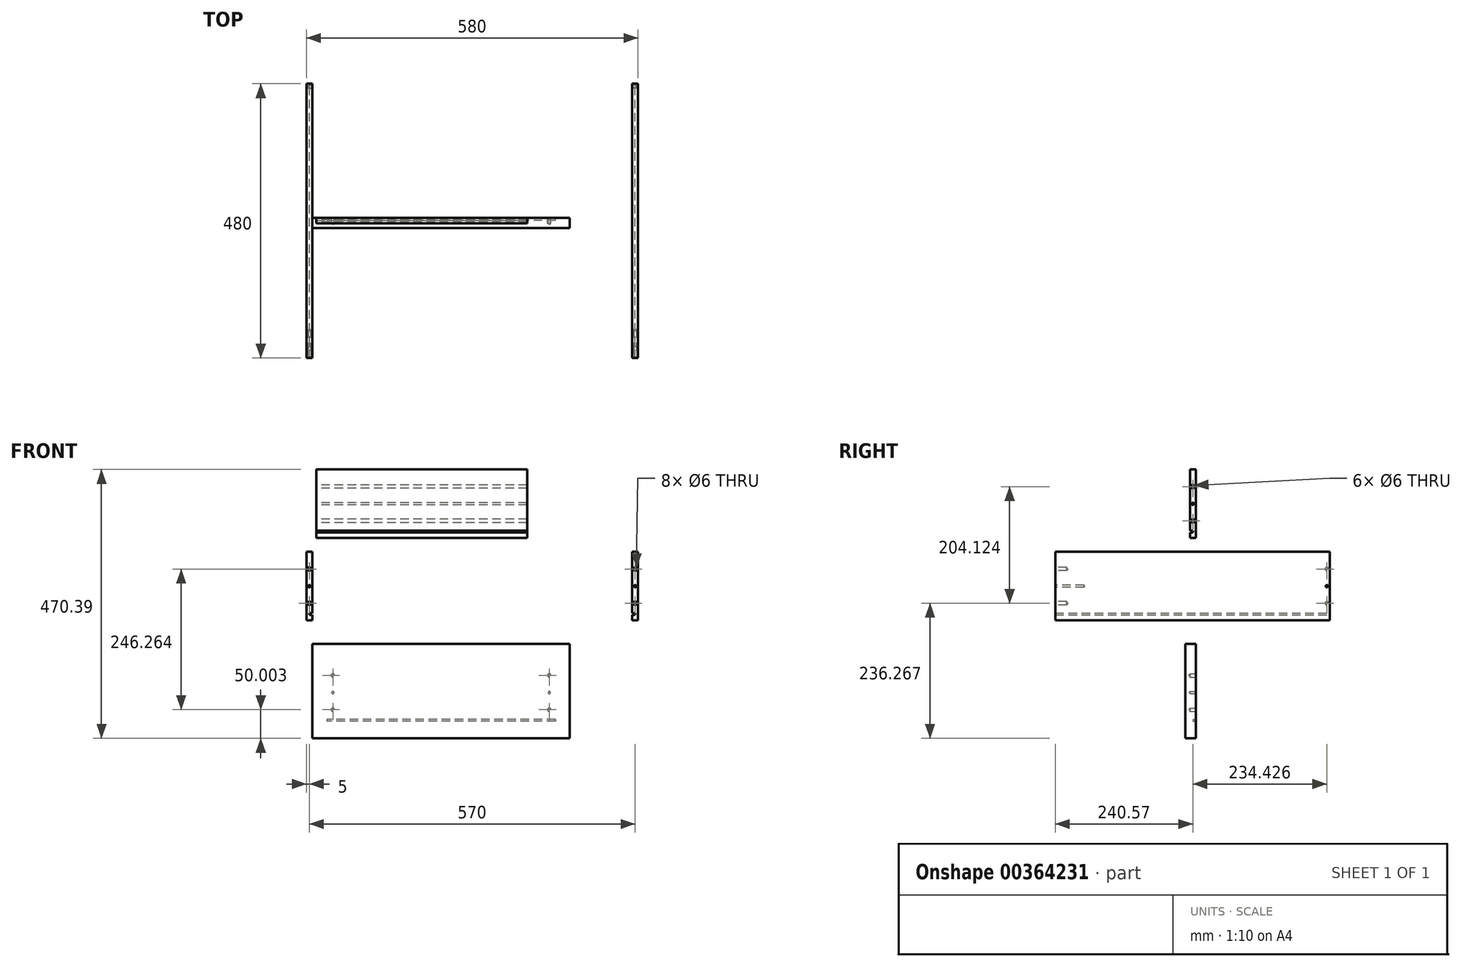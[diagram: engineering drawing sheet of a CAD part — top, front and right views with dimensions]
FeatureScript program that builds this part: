
annotation { "Feature Type Name" : "Feature", "Feature Type Description" : "" }
export const myFeature = defineFeature(function(context is Context, id is Id, definition is map)
    precondition{}
    {
        {
            var Q0;
            Q0=qCreatedBy(makeId("Front.planeOp"),FACE);
            var sketch = newSketch(context, id + "F0", { "sketchPlane" : qUnion([Q0])});
            skLineSegment(sketch, "E0", {"start": v(553.87, 203.2) * mm, "end": v(553.87, 200.2) * mm});
            skText(sketch, "E1", { "text": "Grubość Rowka", "fontName": "OpenSans-Regular.ttf"});
            const initialGuessF0  = {"E1": [0.56755, 0.19197, 1, 0, 0.02]};
            skSetInitialGuess(sketch, initialGuessF0);
            skSolve(sketch);
        }
        {
            var Q0;
            Q0=qCreatedBy(makeId("Right.planeOp"),FACE);
            var sketch = newSketch(context, id + "F1", { "sketchPlane" : qUnion([Q0])});
            skLineSegment(sketch, "E2.bottom", {"start": v(-245.57, 66.34) * mm, "end": v(234.43, 66.34) * mm});
            skLineSegment(sketch, "E2.top", {"start": v(-245.57, -53.66) * mm, "end": v(234.43, -53.66) * mm});
            skLineSegment(sketch, "E2.left", {"start": v(-245.57, 66.34) * mm, "end": v(-245.57, -53.66) * mm});
            skLineSegment(sketch, "E2.right", {"start": v(234.43, 66.34) * mm, "end": v(234.43, -53.66) * mm});
            skSolve(sketch);
        }
        {
            var Q0;
            Q0 = qSketchRegion(id + "F1", true);
            extrude(context, id + "F2", {"entities" : qUnion([Q0]), "depth" : -290 * mm, "hasSecondDirection" : true, "secondDirectionOppositeDirection" : true, "secondDirectionDepth" : 280 * mm});
        }
        {
            var Q0;
            Q0=qCreatedBy(makeId("Right.planeOp"),FACE);
            var sketch = newSketch(context, id + "F3", { "sketchPlane" : qUnion([Q0])});
            skLineSegment(sketch, "E3.bottom", {"start": v(-245.57, -40.66) * mm, "end": v(234.43, -40.66) * mm});
            skLineSegment(sketch, "E3.top", {"start": v(-245.57, -43.66) * mm, "end": v(234.43, -43.66) * mm});
            skLineSegment(sketch, "E3.left", {"start": v(-245.57, -40.66) * mm, "end": v(-245.57, -43.66) * mm});
            skLineSegment(sketch, "E3.right", {"start": v(234.43, -40.66) * mm, "end": v(234.43, -43.66) * mm});
            skSolve(sketch);
        }
        {
            var Q0;
            Q0 = qSketchRegion(id + "F3", true);
            var Q1;
            Q1=makeQuery(id+"F2.opExtrude","CAP_FACE",FACE,{"disambiguationData":[OSD([sQuery(id+"F1.wireOp",EDGE,"E2.bottom"),sQuery(id+"F1.wireOp",EDGE,"E2.top"),sQuery(id+"F1.wireOp",EDGE,"E2.left"),sQuery(id+"F1.wireOp",EDGE,"E2.right")])],"isStart":false});
            extrude(context, id + "F4", {"entities" : qUnion([Q0]), "endBoundEntityFace" : qUnion([Q1]), "depth" : -285 * mm, "hasSecondDirection" : true, "secondDirectionOppositeDirection" : false, "secondDirectionDepth" : -280 * mm});
        }
        {
            var Q0;
            Q0=makeQuery(id+"F4.opExtrude","SWEPT_BODY",BODY,{"disambiguationData":[OSD([sQuery(id+"F3.wireOp",EDGE,"E3.bottom"),sQuery(id+"F3.wireOp",EDGE,"E3.top"),sQuery(id+"F3.wireOp",EDGE,"E3.left"),sQuery(id+"F3.wireOp",EDGE,"E3.right")])]});
            var Q1;
            Q1=makeQuery(id+"F2.opExtrude","SWEPT_BODY",BODY,{"disambiguationData":[OSD([sQuery(id+"F1.wireOp",EDGE,"E2.bottom"),sQuery(id+"F1.wireOp",EDGE,"E2.top"),sQuery(id+"F1.wireOp",EDGE,"E2.left"),sQuery(id+"F1.wireOp",EDGE,"E2.right")])]});
            booleanBodies(context, id + "F5", {"operationType" : BooleanOperationType.SUBTRACTION, "tools" : qUnion([Q0]), "targets" : qUnion([Q1])});
        }
        {
            var Q0;
            Q0=qCreatedBy(makeId("Front.planeOp"),FACE);
            var sketch = newSketch(context, id + "F6", { "sketchPlane" : qUnion([Q0])});
            skLineSegment(sketch, "E4.bottom", {"start": v(-272.58, 210.46) * mm, "end": v(96.02, 210.46) * mm});
            skLineSegment(sketch, "E4.top", {"start": v(-272.58, 90.46) * mm, "end": v(96.02, 90.46) * mm});
            skLineSegment(sketch, "E4.left", {"start": v(-272.58, 210.46) * mm, "end": v(-272.58, 90.46) * mm});
            skLineSegment(sketch, "E4.right", {"start": v(96.02, 210.46) * mm, "end": v(96.02, 90.46) * mm});
            skSolve(sketch);
        }
        {
            var Q0;
            Q0=qCreatedBy(makeId("Front.planeOp"),FACE);
            var sketch = newSketch(context, id + "F7", { "sketchPlane" : qUnion([Q0])});
            skLineSegment(sketch, "E5.bottom", {"start": v(-272.58, 103.46) * mm, "end": v(96.02, 103.46) * mm});
            skLineSegment(sketch, "E5.top", {"start": v(-272.58, 100.46) * mm, "end": v(96.02, 100.46) * mm});
            skLineSegment(sketch, "E5.left", {"start": v(-272.58, 103.46) * mm, "end": v(-272.58, 100.46) * mm});
            skLineSegment(sketch, "E5.right", {"start": v(96.02, 103.46) * mm, "end": v(96.02, 100.46) * mm});
            skSolve(sketch);
        }
        {
            var Q0;
            Q0 = qSketchRegion(id + "F6", true);
            extrude(context, id + "F8", {"entities" : qUnion([Q0]), "depth" : 10 * mm});
        }
        {
            var Q0;
            Q0 = qSketchRegion(id + "F7", true);
            var Q1;
            Q1=makeQuery(id+"F8.opExtrude","SWEPT_FACE",FACE,{"disambiguationData":[OSD([sQuery(id+"F6.wireOp",EDGE,"E4.left")])]});
            extrude(context, id + "F9", {"entities" : qUnion([Q0]), "operationType" : NewBodyOperationType.REMOVE, "depth" : 10 * mm, "hasSecondDirection" : true, "secondDirectionOppositeDirection" : true, "secondDirectionBoundEntityFace" : qUnion([Q1]), "secondDirectionDepth" : -5 * mm});
        }
        {
            var Q0;
            Q0=makeQuery(id+"F8.opExtrude","SWEPT_FACE",FACE,{"disambiguationData":[OSD([sQuery(id+"F6.wireOp",EDGE,"E4.left")])]});
            var sketch = newSketch(context, id + "F10", { "sketchPlane" : qUnion([Q0])});
            skLineSegment(sketch, "E6", {"start": v(0, 198.64) * mm, "end": v(10, 198.64) * mm, "construction": true});
            skPoint(sketch, "E7", {"position": v(5, 198.64) * mm});
            skLineSegment(sketch, "E8", {"start": v(5, 210.46) * mm, "end": v(5, 90.46) * mm});
            skPoint(sketch, "E9", {"position": v(5, 180.46) * mm});
            skPoint(sketch, "E10", {"position": v(5, 120.46) * mm});
            skPoint(sketch, "E11", {"position": v(5, 150.46) * mm});
            skSolve(sketch);
        }
        {
            var Q0;
            Q0=sQuery(id+"F10.wireOp",VERTEX,"E9");
            var Q1;
            Q1=sQuery(id+"F10.wireOp",VERTEX,"E10");
            var Q2;
            Q2=makeQuery(id+"F8.opExtrude","SWEPT_BODY",BODY,{"disambiguationData":[OSD([sQuery(id+"F6.wireOp",EDGE,"E4.bottom"),sQuery(id+"F6.wireOp",EDGE,"E4.top"),sQuery(id+"F6.wireOp",EDGE,"E4.left"),sQuery(id+"F6.wireOp",EDGE,"E4.right")])]});
            hole(context, id + "F11", {"style" : HoleStyle.SIMPLE, "endStyle" : HoleEndStyle.THROUGH, "holeDiameter" : 6 * mm, "isTappedThrough" : true, "tappedDepth" : 12 * mm, "tapClearance" : 3, "startFromSketch" : true, "locations" : qUnion([Q0, Q1]), "scope" : qUnion([Q2])});
        }
        {
            var Q0;
            Q0=sQuery(id+"F10.wireOp",VERTEX,"E11");
            var Q1;
            Q1=makeQuery(id+"F8.opExtrude","SWEPT_BODY",BODY,{"disambiguationData":[OSD([sQuery(id+"F6.wireOp",EDGE,"E4.bottom"),sQuery(id+"F6.wireOp",EDGE,"E4.top"),sQuery(id+"F6.wireOp",EDGE,"E4.left"),sQuery(id+"F6.wireOp",EDGE,"E4.right")])]});
            hole(context, id + "F12", {"style" : HoleStyle.SIMPLE, "endStyle" : HoleEndStyle.THROUGH, "holeDiameter" : 4 * mm, "isTappedThrough" : true, "tappedDepth" : 12 * mm, "tapClearance" : 3, "startFromSketch" : true, "locations" : qUnion([Q0]), "scope" : qUnion([Q1])});
        }
        {
            var Q0;
            {var subQ0=sQuery(id+"F1.wireOp",EDGE,"E2.top");var subQ1=sQuery(id+"F1.wireOp",EDGE,"E2.left");var subQ2=sQuery(id+"F1.wireOp",EDGE,"E2.right");Q0=makeQuery(id+"F5.opBoolean","SPLIT",FACE,{"disambiguationData":[TD([makeQuery(id+"F2.opExtrude","SWEPT_FACE",FACE,{"disambiguationData":[OSD([subQ0])]})])],"derivedFrom":makeQuery(id+"F2.opExtrude","CAP_FACE",FACE,{"disambiguationData":[OSD([sQuery(id+"F1.wireOp",EDGE,"E2.bottom"),subQ0,subQ1,subQ2])],"isStart":true})});}
            var sketch = newSketch(context, id + "F13", { "sketchPlane" : qUnion([Q0])});
            skLineSegment(sketch, "E12", {"start": v(229.43, 66.34) * mm, "end": v(229.43, -53.66) * mm});
            skPoint(sketch, "E13", {"position": v(229.43, 36.34) * mm});
            skPoint(sketch, "E14", {"position": v(229.43, -23.66) * mm});
            skPoint(sketch, "E15", {"position": v(229.43, 6.34) * mm});
            skSolve(sketch);
        }
        {
            var Q0;
            Q0=sQuery(id+"F13.wireOp",VERTEX,"E13");
            var Q1;
            Q1=sQuery(id+"F13.wireOp",VERTEX,"E14");
            var Q2;
            Q2=makeQuery(id+"F2.opExtrude","SWEPT_BODY",BODY,{"disambiguationData":[OSD([sQuery(id+"F1.wireOp",EDGE,"E2.bottom"),sQuery(id+"F1.wireOp",EDGE,"E2.top"),sQuery(id+"F1.wireOp",EDGE,"E2.left"),sQuery(id+"F1.wireOp",EDGE,"E2.right")])]});
            hole(context, id + "F14", {"style" : HoleStyle.SIMPLE, "endStyle" : HoleEndStyle.BLIND, "holeDiameter" : 6 * mm, "holeDepth" : 7 * mm, "isTappedThrough" : true, "tappedDepth" : 12 * mm, "tapClearance" : 3, "startFromSketch" : true, "locations" : qUnion([Q0, Q1]), "scope" : qUnion([Q2])});
        }
        {
            var Q0;
            Q0=sQuery(id+"F13.wireOp",VERTEX,"E15");
            var Q1;
            Q1=makeQuery(id+"F2.opExtrude","SWEPT_BODY",BODY,{"disambiguationData":[OSD([sQuery(id+"F1.wireOp",EDGE,"E2.bottom"),sQuery(id+"F1.wireOp",EDGE,"E2.top"),sQuery(id+"F1.wireOp",EDGE,"E2.left"),sQuery(id+"F1.wireOp",EDGE,"E2.right")])]});
            hole(context, id + "F15", {"style" : HoleStyle.SIMPLE, "endStyle" : HoleEndStyle.THROUGH, "holeDiameter" : 4 * mm, "isTappedThrough" : true, "tappedDepth" : 12 * mm, "tapClearance" : 3, "startFromSketch" : true, "locations" : qUnion([Q0]), "scope" : qUnion([Q1])});
        }
        {
            var Q0;
            Q0=makeQuery(id+"F2.opExtrude","SWEPT_FACE",FACE,{"disambiguationData":[OSD([sQuery(id+"F1.wireOp",EDGE,"E2.left")])]});
            var sketch = newSketch(context, id + "F16", { "sketchPlane" : qUnion([Q0])});
            skLineSegment(sketch, "E16", {"start": v(-285, 66.34) * mm, "end": v(-285, -53.66) * mm});
            skPoint(sketch, "E17", {"position": v(-285, 36.34) * mm});
            skPoint(sketch, "E18", {"position": v(-285, 6.34) * mm});
            skPoint(sketch, "E19", {"position": v(-285, -23.66) * mm});
            skSolve(sketch);
        }
        {
            var Q0;
            Q0=sQuery(id+"F16.wireOp",VERTEX,"E17");
            var Q1;
            Q1=sQuery(id+"F16.wireOp",VERTEX,"E19");
            var Q2;
            Q2=makeQuery(id+"F2.opExtrude","SWEPT_BODY",BODY,{"disambiguationData":[OSD([sQuery(id+"F1.wireOp",EDGE,"E2.bottom"),sQuery(id+"F1.wireOp",EDGE,"E2.top"),sQuery(id+"F1.wireOp",EDGE,"E2.left"),sQuery(id+"F1.wireOp",EDGE,"E2.right")])]});
            hole(context, id + "F17", {"style" : HoleStyle.SIMPLE, "endStyle" : HoleEndStyle.BLIND, "holeDiameter" : 6 * mm, "holeDepth" : 20 * mm, "isTappedThrough" : true, "tappedDepth" : 12 * mm, "tapClearance" : 3, "startFromSketch" : true, "locations" : qUnion([Q0, Q1]), "scope" : qUnion([Q2])});
        }
        {
            var Q0;
            Q0=sQuery(id+"F16.wireOp",VERTEX,"E18");
            var Q1;
            Q1=makeQuery(id+"F2.opExtrude","SWEPT_BODY",BODY,{"disambiguationData":[OSD([sQuery(id+"F1.wireOp",EDGE,"E2.bottom"),sQuery(id+"F1.wireOp",EDGE,"E2.top"),sQuery(id+"F1.wireOp",EDGE,"E2.left"),sQuery(id+"F1.wireOp",EDGE,"E2.right")])]});
            hole(context, id + "F18", {"style" : HoleStyle.SIMPLE, "endStyle" : HoleEndStyle.BLIND, "holeDiameter" : 4 * mm, "holeDepth" : 50 * mm, "isTappedThrough" : true, "tappedDepth" : 12 * mm, "tapClearance" : 3, "startFromSketch" : true, "locations" : qUnion([Q0]), "scope" : qUnion([Q1])});
        }
        {
            var Q0;
            Q0=makeQuery(id+"F2.opExtrude","SWEPT_BODY",BODY,{"disambiguationData":[OSD([sQuery(id+"F1.wireOp",EDGE,"E2.bottom"),sQuery(id+"F1.wireOp",EDGE,"E2.top"),sQuery(id+"F1.wireOp",EDGE,"E2.left"),sQuery(id+"F1.wireOp",EDGE,"E2.right")])]});
            var Q1;
            Q1=qCreatedBy(makeId("Right.planeOp"),FACE);
            mirror(context, id + "F19", {"entities" : qUnion([Q0]), "mirrorPlane" : qUnion([Q1])});
        }
        {
            var Q0;
            Q0=qCreatedBy(makeId("Front.planeOp"),FACE);
            var sketch = newSketch(context, id + "F20", { "sketchPlane" : qUnion([Q0])});
            skLineSegment(sketch, "E20.bottom", {"start": v(-279.57, -94.93) * mm, "end": v(170.43, -94.93) * mm});
            skLineSegment(sketch, "E20.top", {"start": v(-279.57, -259.93) * mm, "end": v(170.43, -259.93) * mm});
            skLineSegment(sketch, "E20.left", {"start": v(-279.57, -94.93) * mm, "end": v(-279.57, -259.93) * mm});
            skLineSegment(sketch, "E20.right", {"start": v(170.43, -94.93) * mm, "end": v(170.43, -259.93) * mm});
            skSolve(sketch);
        }
        {
            var Q0;
            Q0=makeQuery(id+"F20.imprint","IMPRINT",FACE,{"disambiguationData":[TD([[makeQuery(id+"F20.imprint","IMPRINT",EDGE,{"derivedFrom":sQuery(id+"F20.wireOp",EDGE,"E20.bottom")}),-1.0]])]});
            var sketch = newSketch(context, id + "F21", { "sketchPlane" : qUnion([Q0])});
            skLineSegment(sketch, "E21.bottom", {"start": v(-279.57, -226.93) * mm, "end": v(170.43, -226.93) * mm, "construction": true});
            skLineSegment(sketch, "E21.top", {"start": v(-279.57, -229.93) * mm, "end": v(170.43, -229.93) * mm, "construction": true});
            skLineSegment(sketch, "E21.left", {"start": v(-279.57, -226.93) * mm, "end": v(-279.57, -229.93) * mm, "construction": true});
            skLineSegment(sketch, "E21.right", {"start": v(170.43, -226.93) * mm, "end": v(170.43, -229.93) * mm, "construction": true});
            skLineSegment(sketch, "E22.bottom", {"start": v(145.43, -226.93) * mm, "end": v(-254.57, -226.93) * mm});
            skLineSegment(sketch, "E22.top", {"start": v(145.43, -229.93) * mm, "end": v(-254.57, -229.93) * mm});
            skLineSegment(sketch, "E22.left", {"start": v(145.43, -226.93) * mm, "end": v(145.43, -229.93) * mm});
            skLineSegment(sketch, "E22.right", {"start": v(-254.57, -226.93) * mm, "end": v(-254.57, -229.93) * mm});
            skSolve(sketch);
        }
        {
            var Q0;
            Q0 = qSketchRegion(id + "F20", true);
            extrude(context, id + "F22", {"entities" : qUnion([Q0]), "depth" : 18 * mm});
        }
        {
            var Q0;
            Q0 = qSketchRegion(id + "F21", true);
            extrude(context, id + "F23", {"entities" : qUnion([Q0]), "operationType" : NewBodyOperationType.REMOVE, "depth" : 5 * mm});
        }
        {
            var Q0;
            {var subQ0=sQuery(id+"F20.wireOp",EDGE,"E20.bottom");var subQ1=sQuery(id+"F20.wireOp",EDGE,"E20.right");var subQ2=sQuery(id+"F20.wireOp",EDGE,"E20.left");Q0=makeQuery(id+"F23.boolean.opBoolean","SPLIT",FACE,{"disambiguationData":[TD([makeQuery(id+"F22.opExtrude","SWEPT_FACE",FACE,{"disambiguationData":[OSD([subQ0])]})])],"derivedFrom":makeQuery(id+"F22.opExtrude","CAP_FACE",FACE,{"disambiguationData":[OSD([subQ0,sQuery(id+"F20.wireOp",EDGE,"E20.top"),subQ2,subQ1])],"isStart":true})});}
            var sketch = newSketch(context, id + "F24", { "sketchPlane" : qUnion([Q0])});
            skLineSegment(sketch, "E23", {"start": v(243.87, -94.93) * mm, "end": v(243.87, -259.93) * mm, "construction": true});
            skPoint(sketch, "E24", {"position": v(243.87, -149.93) * mm});
            skPoint(sketch, "E25", {"position": v(243.87, -179.93) * mm});
            skPoint(sketch, "E26", {"position": v(243.87, -209.93) * mm});
            skLineSegment(sketch, "E27", {"start": v(54.57, -94.93) * mm, "end": v(54.57, -259.26) * mm, "construction": true});
            skPoint(sketch, "E28.MirrorP", {"position": v(-134.73, -149.93) * mm});
            skLineSegment(sketch, "E29.MirrorCS", {"start": v(-134.73, -94.93) * mm, "end": v(-134.73, -259.93) * mm, "construction": true});
            skPoint(sketch, "E30.MirrorP", {"position": v(-134.73, -179.93) * mm});
            skPoint(sketch, "E31.MirrorP", {"position": v(-134.73, -209.93) * mm});
            skSolve(sketch);
        }
        {
            var Q0;
            Q0=sQuery(id+"F24.wireOp",VERTEX,"E28.MirrorP");
            var Q1;
            Q1=sQuery(id+"F24.wireOp",VERTEX,"E31.MirrorP");
            var Q2;
            Q2=sQuery(id+"F24.wireOp",VERTEX,"E26");
            var Q3;
            Q3=sQuery(id+"F24.wireOp",VERTEX,"E24");
            var Q4;
            Q4=makeQuery(id+"F22.opExtrude","SWEPT_BODY",BODY,{"disambiguationData":[OSD([sQuery(id+"F20.wireOp",EDGE,"E20.bottom"),sQuery(id+"F20.wireOp",EDGE,"E20.top"),sQuery(id+"F20.wireOp",EDGE,"E20.left"),sQuery(id+"F20.wireOp",EDGE,"E20.right")])]});
            hole(context, id + "F25", {"style" : HoleStyle.SIMPLE, "endStyle" : HoleEndStyle.BLIND, "holeDiameter" : 6 * mm, "holeDepth" : 10 * mm, "isTappedThrough" : true, "tappedDepth" : 12 * mm, "tapClearance" : 3, "startFromSketch" : true, "locations" : qUnion([Q0, Q1, Q2, Q3]), "scope" : qUnion([Q4])});
        }
        {
            var Q0;
            Q0=sQuery(id+"F24.wireOp",VERTEX,"E30.MirrorP");
            var Q1;
            Q1=sQuery(id+"F24.wireOp",VERTEX,"E25");
            var Q2;
            Q2=makeQuery(id+"F22.opExtrude","SWEPT_BODY",BODY,{"disambiguationData":[OSD([sQuery(id+"F20.wireOp",EDGE,"E20.bottom"),sQuery(id+"F20.wireOp",EDGE,"E20.top"),sQuery(id+"F20.wireOp",EDGE,"E20.left"),sQuery(id+"F20.wireOp",EDGE,"E20.right")])]});
            hole(context, id + "F26", {"style" : HoleStyle.SIMPLE, "endStyle" : HoleEndStyle.BLIND, "holeDiameter" : 4 * mm, "holeDepth" : 10 * mm, "isTappedThrough" : true, "tappedDepth" : 12 * mm, "tapClearance" : 3, "startFromSketch" : true, "locations" : qUnion([Q0, Q1]), "scope" : qUnion([Q2])});
        }
    });
